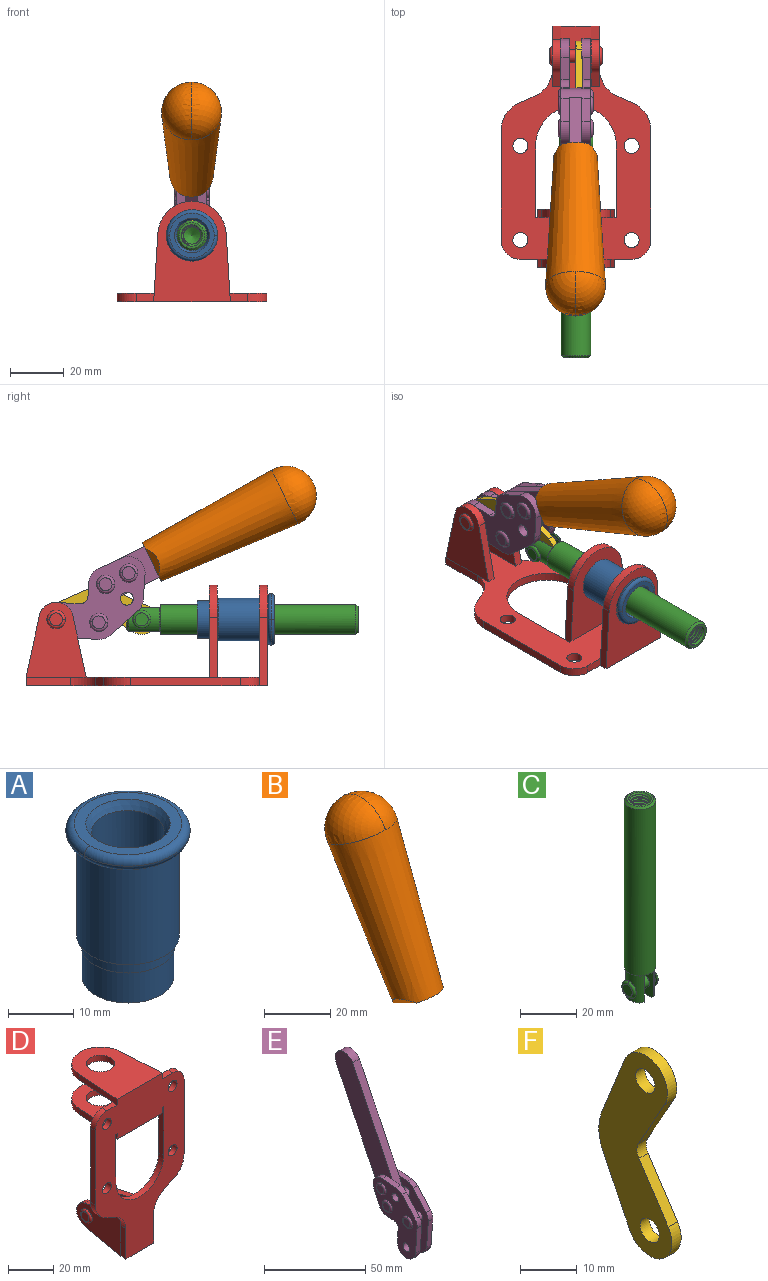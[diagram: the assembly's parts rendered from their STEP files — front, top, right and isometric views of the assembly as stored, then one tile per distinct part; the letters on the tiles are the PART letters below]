
ASSEMBLY  parts=6 mates=7
PART A: 15 faces, bbox 20.6x20.6x28.7 mm
  f0: torus R=8.26mm, axis (0,0,1), area 56.8mm2, adj f1,f10,f12
  f1: torus R=8.26mm, axis (0,0,1), area 56.8mm2, adj f0,f6,f13
  f2: cylinder r=5.59mm len=25.91mm, axis (0,0,1), area 909.6mm2, adj f3,f4
  f3: cone r=6.86mm half-angle=45deg, axis (0,0,-1), area 70.2mm2, adj f2,f14
  f4: cone r=6.47mm half-angle=30deg, axis (0,0,1), area 66.7mm2, adj f2,f13
  f5: cylinder r=7.04mm len=14.07mm, axis (0,0,1), area 252.6mm2, adj f11,f14
  f6: torus R=8.26mm, axis (0,0,1), area 56.8mm2, adj f1,f12,f13
  f7: cylinder r=7.16mm len=14.33mm, axis (0,0,1), area 91.5mm2, adj f9,f11
  f8: cylinder r=7.86mm len=18.42mm, axis (0,0,1), area 909.6mm2, adj f9,f10
  f9: plane 15.72x15.72mm, normal (0,0,-1), area 33mm2, adj f7,f8
  f10: plane 16.51x16.51mm, normal (0,0,-1), area 19.9mm2, adj f0,f8,f12
  f11: plane 14.33x14.33mm, normal (0,0,-1), area 5.7mm2, adj f5,f7
  f12: torus R=8.26mm, axis (0,0,1), area 56.8mm2, adj f0,f6,f10
  f13: plane 16.51x16.51mm, normal (0,0,1), area 82.7mm2, adj f1,f4,f6
  f14: plane 14.07x14.07mm, normal (0,0,-1), area 7.8mm2, adj f3,f5
PART B: 11 faces, bbox 22.3x42.6x64.5 mm
  f0: sphere r=11.13mm, area 411.4mm2, adj f1,f8
  f1: cone r=11.11mm half-angle=3.3deg, axis (0,0.44,0.9), area 3251.8mm2, adj f0,f7,f8,f9,f10
  f2: cylinder r=6.16mm len=11.7mm, axis (1,0,0), area 89.5mm2, adj f3,f4,f5,f6
  f3: plane 60.23x36.75mm, normal (-1,0,0), area 763.6mm2, adj f2,f4,f6,f10
  f4: plane 51.37x25.05mm, normal (0,0.9,-0.44), area 264.2mm2, adj f2,f3,f5,f10
  f5: plane 60.23x36.75mm, normal (1,0,0), area 763.6mm2, adj f2,f4,f6,f10
  f6: plane 51.37x25.05mm, normal (0,-0.9,0.44), area 264.2mm2, adj f2,f3,f5,f10
  f7: plane 9.95x5.95mm, normal (0.71,-0.31,-0.64), area 25.8mm2, adj f1,f10
  f8: sphere r=11.13mm, area 411.4mm2, adj f0,f1
  f9: plane 9.95x5.95mm, normal (-0.71,-0.31,-0.64), area 25.8mm2, adj f1,f10
  f10: plane 14.27x11.38mm, normal (0,-0.44,-0.9), area 106.7mm2, adj f1,f3,f4,f5,f6,f7,f9
PART C: 48 faces, bbox 12.6x11.1x86.1 mm
  f0: torus R=2.41mm, axis (-1,0,0), area 15mm2, adj f30,f32,f34
  f1: torus R=2.41mm, axis (-1,0,0), area 15mm2, adj f29,f31,f33
  f2: cylinder r=5.54mm len=72.39mm, axis (0,0,1), area 2518.5mm2, adj f3,f4,f42,f43
  f3: cone r=5.54mm half-angle=45deg, axis (0,0,1), area 7.6mm2, adj f2,f5,f41
  f4: cone r=5.54mm half-angle=45deg, axis (0,0,-1), area 34.9mm2, adj f2,f39
  f5: cylinder r=5.08mm len=11.48mm, axis (0,0,1), area 108.3mm2, adj f3,f7,f8,f41
  f6: cylinder r=2.41mm len=4.83mm, axis (-1,0,0), area 71.2mm2, adj f40,f41
  f7: cylinder r=2.41mm len=4.83mm, axis (-1,0,0), area 7.6mm2, adj f5,f34
  f8: cone r=5.08mm half-angle=45deg, axis (0,0,1), area 10.6mm2, adj f5,f37,f41
  f9: cone r=3.98mm half-angle=45deg, axis (0,0,1), area 17.6mm2, adj f27,f39,f45,f46,f47
  f10: cylinder r=2.41mm len=4.83mm, axis (-1,0,0), area 7.6mm2, adj f33,f38
  f11: cylinder r=3.2mm len=6.4mm, axis (0,0,1), area 78.4mm2, adj f12,f28,f44,f45,f47
  f12: cylinder r=3.2mm len=6.4mm, axis (0,0,1), area 10.5mm2, adj f11,f13,f45,f47
  f13: cylinder r=3.2mm len=6.4mm, axis (0,0,1), area 10.5mm2, adj f12,f14,f45,f47
  f14: cylinder r=3.2mm len=6.4mm, axis (0,0,1), area 10.5mm2, adj f13,f15,f45,f47
  f15: cylinder r=3.2mm len=6.4mm, axis (0,0,1), area 10.5mm2, adj f14,f16,f45,f47
  f16: cylinder r=3.2mm len=6.4mm, axis (0,0,1), area 10.5mm2, adj f15,f17,f45,f47
  f17: cylinder r=3.2mm len=6.4mm, axis (0,0,1), area 10.5mm2, adj f16,f18,f45,f47
  f18: cylinder r=3.2mm len=6.4mm, axis (0,0,1), area 10.5mm2, adj f17,f19,f45,f47
  f19: cylinder r=3.2mm len=6.4mm, axis (0,0,1), area 10.5mm2, adj f18,f20,f45,f47
  f20: cylinder r=3.2mm len=6.4mm, axis (0,0,1), area 10.5mm2, adj f19,f21,f45,f47
  f21: cylinder r=3.2mm len=6.4mm, axis (0,0,1), area 10.5mm2, adj f20,f22,f45,f47
  f22: cylinder r=3.2mm len=6.4mm, axis (0,0,1), area 10.5mm2, adj f21,f23,f45,f47
  f23: cylinder r=3.2mm len=6.4mm, axis (0,0,1), area 10.5mm2, adj f22,f24,f45,f47
  f24: cylinder r=3.2mm len=6.4mm, axis (0,0,1), area 10.5mm2, adj f23,f25,f45,f47
  f25: cylinder r=3.2mm len=6.4mm, axis (0,0,1), area 10.5mm2, adj f24,f26,f45,f47
  f26: cylinder r=3.2mm len=6.4mm, axis (0,0,1), area 10.5mm2, adj f25,f27,f45,f47
  f27: cylinder r=3.2mm len=6.4mm, axis (0,0,1), area 7.4mm2, adj f9,f26,f45,f47
  f28: cone r=3.2mm half-angle=60deg, axis (0,0,1), area 37.2mm2, adj f11
  f29: plane 4.83x4.83mm, normal (-1,0,0), area 18.3mm2, adj f1,f31
  f30: plane 4.83x4.83mm, normal (1,0,0), area 18.3mm2, adj f0,f32
  f31: torus R=2.41mm, axis (-1,0,0), area 15mm2, adj f1,f29,f33
  f32: torus R=2.41mm, axis (-1,0,0), area 15mm2, adj f0,f30,f34
  f33: plane 6.83x6.83mm, normal (1,0,0), area 18.3mm2, adj f1,f10,f31
  f34: plane 6.83x6.83mm, normal (-1,0,0), area 18.3mm2, adj f0,f7,f32
  f35: cone r=5.08mm half-angle=45deg, axis (0,0,1), area 10.6mm2, adj f36,f38,f40
  f36: plane 7.25x1.97mm, normal (0,0,-1), area 10mm2, adj f35,f40
  f37: plane 7.25x1.97mm, normal (0,0,-1), area 10mm2, adj f8,f41
  f38: cylinder r=5.08mm len=11.48mm, axis (0,0,1), area 108.3mm2, adj f10,f35,f40,f42
  f39: plane 9.55x9.55mm, normal (0,0,1), area 22mm2, adj f4,f9
  f40: plane 12.76x10.09mm, normal (1,0,0), area 95.7mm2, adj f6,f35,f36,f38,f42,f43
  f41: plane 12.76x10.09mm, normal (-1,0,0), area 95.7mm2, adj f3,f5,f6,f8,f37,f43
  f42: cone r=5.54mm half-angle=45deg, axis (0,0,1), area 7.6mm2, adj f2,f38,f40
  f43: plane 11.07x4.7mm, normal (0,0,-1), area 50.4mm2, adj f2,f40,f41
  f44: plane 0.89x0.62mm, normal (-1,0,0), area 0.3mm2, adj f11,f45,f46,f47
  f45: bspline ~24.8x7.63mm, area 266.6mm2, adj f9,f11,f12,f13,f14,f15,f16,f17
  f46: bspline ~24.87x7.63mm, area 73.6mm2, adj f9,f44,f45,f47
  f47: bspline ~24.98x7.63mm, area 272.5mm2, adj f9,f11,f12,f13,f14,f15,f16,f17
PART D: 55 faces, bbox 55.7x37.4x89.8 mm
  f0: torus R=2.41mm, axis (-1,0,0), area 15mm2, adj f11,f15,f25
  f1: torus R=2.41mm, axis (-1,0,0), area 15mm2, adj f10,f12,f22
  f2: cylinder r=2.78mm len=5.56mm, axis (0,-1,0), area 54.2mm2, adj f30,f54
  f3: cylinder r=14.99mm len=29.97mm, axis (0,-1,0), area 145.9mm2, adj f30,f49,f53,f54
  f4: cylinder r=2.78mm len=5.56mm, axis (0,-1,0), area 54.2mm2, adj f30,f54
  f5: cylinder r=2.78mm len=5.56mm, axis (0,-1,0), area 54.2mm2, adj f30,f54
  f6: cylinder r=2.78mm len=5.56mm, axis (0,-1,0), area 54.2mm2, adj f30,f54
  f7: cylinder r=6.35mm len=12.7mm, axis (0,0,1), area 123.6mm2, adj f27,f51
  f8: cylinder r=6.35mm len=12.7mm, axis (0,0,-1), area 124.7mm2, adj f21,f35
  f9: cylinder r=2.41mm len=11.18mm, axis (-1,0,0), area 169.4mm2, adj f16,f19
  f10: plane 4.83x4.83mm, normal (1,0,0), area 18.3mm2, adj f1,f12
  f11: plane 4.83x4.83mm, normal (-1,0,0), area 18.3mm2, adj f0,f15
  f12: torus R=2.41mm, axis (-1,0,0), area 15mm2, adj f1,f10,f22
  f13: cylinder r=6.35mm len=12.41mm, axis (1,0,0), area 53.4mm2, adj f18,f19,f22,f23
  f14: cylinder r=6.35mm len=12.41mm, axis (-1,0,0), area 53.4mm2, adj f16,f17,f24,f25
  f15: torus R=2.41mm, axis (-1,0,0), area 15mm2, adj f0,f11,f25
  f16: plane 27.86x22.35mm, normal (1,0,0), area 425.4mm2, adj f9,f14,f17,f24,f30
  f17: plane 22.86x4.97mm, normal (0,0.21,0.98), area 72.5mm2, adj f14,f16,f25,f30
  f18: plane 22.86x4.97mm, normal (0,0.21,0.98), area 72.5mm2, adj f13,f19,f22,f30
  f19: plane 27.86x22.35mm, normal (-1,0,0), area 425.4mm2, adj f9,f13,f18,f23,f30
  f20: cylinder r=12.7mm len=25.35mm, axis (0,0,-1), area 119.8mm2, adj f21,f34,f35,f36
  f21: plane 34.21x28.07mm, normal (0,0,-1), area 702.4mm2, adj f8,f20,f30,f34,f36
  f22: plane 27.96x22.45mm, normal (1,0,0), area 407.2mm2, adj f1,f12,f13,f18,f23,f30,f42,f43
  f23: plane 22.86x4.97mm, normal (0,0.21,-0.98), area 72.5mm2, adj f13,f19,f22,f44
  f24: plane 22.86x4.97mm, normal (0,0.21,-0.98), area 72.5mm2, adj f14,f16,f25,f44
  f25: plane 27.86x22.35mm, normal (-1,0,0), area 407.1mm2, adj f0,f14,f15,f17,f24,f30,f45,f46
  f26: plane 3.1x0.95mm, normal (0,0,-1), area 2.7mm2, adj f30,f49,f50,f54
  f27: plane 34.21x28.07mm, normal (0,0,1), area 702.4mm2, adj f7,f28,f30,f50,f52
  f28: cylinder r=12.7mm len=25.35mm, axis (0,0,1), area 118.8mm2, adj f27,f50,f51,f52
  f29: plane 3.1x0.95mm, normal (0,0,-1), area 2.7mm2, adj f30,f52,f53,f54
  f30: plane 86.54x55.63mm, normal (0,1,0), area 2362.9mm2, adj f2,f3,f4,f5,f6,f16,f17,f18
  f31: plane 40.56x3.1mm, normal (-1,0,0), area 125.7mm2, adj f30,f32,f48,f54
  f32: cylinder r=7.11mm len=7.11mm, axis (0,-1,0), area 34.6mm2, adj f30,f31,f33,f54
  f33: plane 6.67x3.1mm, normal (0,0,1), area 20.4mm2, adj f30,f32,f34,f54
  f34: plane 25.39x3.13mm, normal (-1,0.06,0), area 79.5mm2, adj f20,f21,f33,f35,f54
  f35: plane 37.31x28.45mm, normal (0,0,1), area 789.9mm2, adj f8,f20,f34,f36,f54
  f36: plane 25.39x3.13mm, normal (1,0.06,0), area 79.5mm2, adj f20,f21,f35,f37,f54
  f37: plane 6.67x3.1mm, normal (0,0,1), area 20.4mm2, adj f30,f36,f38,f54
  f38: cylinder r=7.11mm len=7.11mm, axis (0,-1,0), area 34.6mm2, adj f30,f37,f39,f54
  f39: plane 40.56x3.1mm, normal (1,0,0), area 125.7mm2, adj f30,f38,f40,f54
  f40: cylinder r=11.18mm len=10.16mm, axis (0,-1,0), area 39.5mm2, adj f30,f39,f41,f54
  f41: plane 6.09x3.1mm, normal (0.42,0,-0.91), area 20.8mm2, adj f30,f40,f42,f54
  f42: cylinder r=11.18mm len=9.41mm, axis (0,-1,0), area 37.2mm2, adj f22,f30,f41,f43,f54
  f43: plane 16.5x3.1mm, normal (1,0,0), area 51.1mm2, adj f22,f42,f44,f54
  f44: plane 17.37x3.1mm, normal (0,0,-1), area 53.8mm2, adj f23,f24,f30,f43,f45,f54
  f45: plane 16.5x3.1mm, normal (-1,0,0), area 51.1mm2, adj f25,f44,f46,f54
  f46: cylinder r=11.18mm len=9.41mm, axis (0,-1,0), area 37.2mm2, adj f25,f30,f45,f47,f54
  f47: plane 6.09x3.1mm, normal (-0.42,0,-0.91), area 20.8mm2, adj f30,f46,f48,f54
  f48: cylinder r=11.18mm len=10.16mm, axis (0,-1,0), area 39.5mm2, adj f30,f31,f47,f54
  f49: plane 26.54x3.1mm, normal (-1,0,0), area 82.3mm2, adj f3,f26,f30,f54
  f50: plane 25.39x3.1mm, normal (1,0.06,0), area 78.8mm2, adj f26,f27,f28,f51,f54
  f51: plane 37.31x28.45mm, normal (0,0,-1), area 789.9mm2, adj f7,f28,f50,f52,f54
  f52: plane 25.39x3.1mm, normal (-1,0.06,0), area 78.8mm2, adj f27,f28,f29,f51,f54
  f53: plane 26.54x3.1mm, normal (1,0,0), area 82.3mm2, adj f3,f29,f30,f54
  f54: plane 89.66x55.63mm, normal (0,-1,0), area 2678.5mm2, adj f2,f3,f4,f5,f6,f26,f29,f31
PART E: 59 faces, bbox 12.9x60.2x99.6 mm
  f0: torus R=2.39mm, axis (-1,0,0), area 14.9mm2, adj f20,f43,f51
  f1: torus R=2.39mm, axis (-1,0,0), area 14.9mm2, adj f19,f42,f51
  f2: torus R=2.39mm, axis (-1,0,0), area 14.9mm2, adj f18,f35,f51
  f3: torus R=2.39mm, axis (-1,0,0), area 14.9mm2, adj f14,f17,f23
  f4: torus R=2.39mm, axis (-1,0,0), area 14.9mm2, adj f13,f16,f23
  f5: torus R=2.39mm, axis (-1,0,0), area 14.9mm2, adj f12,f15,f23
  f6: cylinder r=2.39mm len=4.78mm, axis (1,0,0), area 46.5mm2, adj f48,f50,f51
  f7: cylinder r=2.39mm len=4.78mm, axis (1,0,0), area 46.5mm2, adj f50,f51
  f8: cylinder r=6.35mm len=12.68mm, axis (1,0,0), area 61.8mm2, adj f38,f39,f50,f51
  f9: cylinder r=2.39mm len=4.78mm, axis (-1,0,0), area 70.5mm2, adj f46,f50
  f10: cylinder r=2.39mm len=4.78mm, axis (-1,0,0), area 46.5mm2, adj f23,f45,f46
  f11: cylinder r=2.39mm len=4.78mm, axis (-1,0,0), area 46.5mm2, adj f23,f46
  f12: plane 4.78x4.78mm, normal (1,0,0), area 17.9mm2, adj f5,f15
  f13: plane 4.78x4.78mm, normal (1,0,0), area 17.9mm2, adj f4,f16
  f14: plane 4.78x4.78mm, normal (1,0,0), area 17.9mm2, adj f3,f17
  f15: torus R=2.39mm, axis (-1,0,0), area 14.9mm2, adj f5,f12,f23
  f16: torus R=2.39mm, axis (-1,0,0), area 14.9mm2, adj f4,f13,f23
  f17: torus R=2.39mm, axis (-1,0,0), area 14.9mm2, adj f3,f14,f23
  f18: plane 4.78x4.78mm, normal (-1,0,0), area 17.9mm2, adj f2,f35
  f19: plane 4.78x4.78mm, normal (-1,0,0), area 17.9mm2, adj f1,f42
  f20: plane 4.78x4.78mm, normal (-1,0,0), area 17.9mm2, adj f0,f43
  f21: plane 2.26x0.2mm, normal (1,0,0), area 0.2mm2, adj f31,f44
  f22: plane 2.26x0.2mm, normal (-1,0,0), area 0.2mm2, adj f41,f44
  f23: plane 39.37x30.77mm, normal (1,0,0), area 565.5mm2, adj f3,f4,f5,f10,f11,f15,f16,f17
  f24: cylinder r=6.1mm len=4.15mm, axis (-1,0,0), area 14.7mm2, adj f23,f25,f32,f46
  f25: plane 10.25x9.01mm, normal (0,-0.75,0.66), area 42.3mm2, adj f23,f24,f26,f46
  f26: cylinder r=6.35mm len=4.64mm, axis (-1,0,0), area 15.6mm2, adj f23,f25,f27,f46
  f27: plane 15.84x3.1mm, normal (0,-1,-0.07), area 49.2mm2, adj f23,f26,f28,f46
  f28: cylinder r=6.35mm len=12.68mm, axis (-1,0,0), area 61.8mm2, adj f23,f27,f29,f46
  f29: plane 8.11x3.1mm, normal (0,1,0.07), area 25.2mm2, adj f23,f28,f30,f46
  f30: cylinder r=3.05mm len=3.25mm, axis (-1,0,0), area 14.8mm2, adj f23,f29,f31,f46
  f31: plane 5.99x3.1mm, normal (0,0.07,-1), area 18.6mm2, adj f21,f23,f30,f44,f46
  f32: plane 9.5x3.1mm, normal (0,-0.07,1), area 29.5mm2, adj f23,f24,f33,f46,f47
  f33: cylinder r=6.1mm len=8.63mm, axis (-1,0,0), area 39.1mm2, adj f23,f32,f34,f47
  f34: plane 8.65x3.96mm, normal (0,0.91,-0.42), area 29.5mm2, adj f23,f33,f44,f47
  f35: torus R=2.39mm, axis (-1,0,0), area 14.9mm2, adj f2,f18,f51
  f36: plane 10.25x9.01mm, normal (0,-0.75,0.66), area 42.3mm2, adj f37,f49,f50,f51
  f37: cylinder r=6.35mm len=4.64mm, axis (1,0,0), area 15.6mm2, adj f36,f38,f50,f51
  f38: plane 15.84x3.1mm, normal (0,-1,-0.07), area 49.2mm2, adj f8,f37,f50,f51
  f39: plane 8.11x3.1mm, normal (0,1,0.07), area 25.2mm2, adj f8,f40,f50,f51
  f40: cylinder r=3.05mm len=3.25mm, axis (1,0,0), area 14.8mm2, adj f39,f41,f50,f51
  f41: plane 5.99x3.1mm, normal (0,0.07,-1), area 18.6mm2, adj f22,f40,f44,f50,f51
  f42: torus R=2.39mm, axis (-1,0,0), area 14.9mm2, adj f1,f19,f51
  f43: torus R=2.39mm, axis (-1,0,0), area 14.9mm2, adj f0,f20,f51
  f44: cylinder r=6.35mm len=12.12mm, axis (-1,0,0), area 128.9mm2, adj f21,f22,f23,f31,f34,f41,f46,f47
  f45: plane 2.65x1.35mm, normal (1,0,0), area 1mm2, adj f10,f55
  f46: plane 39.08x20.42mm, normal (-1,0,0), area 412.5mm2, adj f9,f10,f11,f24,f25,f26,f27,f28
  f47: plane 77.62x39.82mm, normal (1,0,0), area 850mm2, adj f32,f33,f34,f44,f53,f54,f55
  f48: plane 2.65x1.35mm, normal (-1,0,0), area 1mm2, adj f6,f55
  f49: cylinder r=6.1mm len=4.15mm, axis (1,0,0), area 14.7mm2, adj f36,f50,f51,f56
  f50: plane 39.08x20.42mm, normal (1,0,0), area 412.5mm2, adj f6,f7,f8,f9,f36,f37,f38,f39
  f51: plane 39.37x30.77mm, normal (-1,0,0), area 565.5mm2, adj f0,f1,f2,f6,f7,f8,f35,f36
  f52: plane 8.65x3.96mm, normal (0,0.91,-0.42), area 29.5mm2, adj f44,f51,f57,f58
  f53: plane 68.49x33.4mm, normal (0,0.9,-0.44), area 358.1mm2, adj f44,f47,f54,f58
  f54: cylinder r=6.35mm len=12.06mm, axis (1,0,0), area 93.7mm2, adj f47,f53,f55,f58
  f55: plane 68.49x33.4mm, normal (0,-0.9,0.44), area 358.1mm2, adj f44,f45,f46,f47,f48,f50,f54,f58
  f56: plane 9.5x3.1mm, normal (0,-0.07,1), area 29.5mm2, adj f49,f50,f51,f57,f58
  f57: cylinder r=6.1mm len=8.63mm, axis (1,0,0), area 39.1mm2, adj f51,f52,f56,f58
  f58: plane 77.62x39.82mm, normal (-1,0,0), area 850mm2, adj f44,f52,f53,f54,f55,f56,f57
PART F: 12 faces, bbox 2.3x18.2x42.8 mm
  f0: cylinder r=2.4mm len=4.8mm, axis (1,0,0), area 34.9mm2, adj f4,f11
  f1: cylinder r=10.41mm len=8.47mm, axis (1,0,0), area 20.2mm2, adj f4,f9,f10,f11
  f2: cylinder r=3.05mm len=3.16mm, axis (1,0,0), area 7.7mm2, adj f4,f6,f7,f11
  f3: cylinder r=2.4mm len=4.8mm, axis (1,0,0), area 34.9mm2, adj f4,f11
  f4: plane 42.81x18.23mm, normal (-1,0,0), area 414.1mm2, adj f0,f1,f2,f3,f5,f6,f7,f8
  f5: cylinder r=5.54mm len=10.67mm, axis (1,0,0), area 41.8mm2, adj f4,f6,f10,f11
  f6: plane 11.66x6.53mm, normal (0,-0.87,-0.49), area 30.9mm2, adj f2,f4,f5,f11
  f7: plane 11.17x7.33mm, normal (0,-0.84,0.55), area 30.9mm2, adj f2,f4,f8,f11
  f8: cylinder r=5.54mm len=10.51mm, axis (1,0,0), area 41.8mm2, adj f4,f7,f9,f11
  f9: plane 13.67x6.67mm, normal (0,0.9,-0.44), area 35.1mm2, adj f1,f4,f8,f11
  f10: plane 14.1x5.7mm, normal (0,0.93,0.37), area 35.1mm2, adj f1,f4,f5,f11
  f11: plane 42.81x18.23mm, normal (1,0,0), area 414.1mm2, adj f0,f1,f2,f3,f5,f6,f7,f8
PLACE A rot(axis=(1,0,0),90deg) t=(0,9.43,0)mm
PLACE B rot(axis=(1,0,0),90deg) t=(-0.18,9.43,0)mm
PLACE C rot(axis=(1,0,0),90deg) t=(0,25.25,0)mm
PLACE D rot(axis=(1,0,0),90deg) t=(0,9.43,0)mm fixed
PLACE E rot(axis=(1,0,0),90deg) t=(-0.14,9.43,0)mm
PLACE F rot(axis=(1,0,0),92deg) t=(1.16,26.1,0.55)mm
MATE fastened A.f2 <-> D.f7  axis (0,1,0) through (0,-36.96,24.61)mm
MATE fastened D.f19 <-> E.f23  axis (-1,0,0) through (5.59,41.52,14.55)mm
MATE slider C.f2 <-> A.f2  axis (0,-1,0) through (0,-33.53,24.61)mm
MATE revolute F.f3 <-> D.f0  axis (1,0,0) through (0,41.52,24.61)mm
MATE revolute E.f7 <-> D.f0  axis (-1,0,0) through (-5.59,41.52,24.61)mm
MATE fastened E.f54 <-> B.f2  axis (-1,0,0) through (-2.49,-45.34,71.04)mm
MATE revolute F.f0 <-> C.f6  axis (-1,0,0) through (0,9.77,24.61)mm
